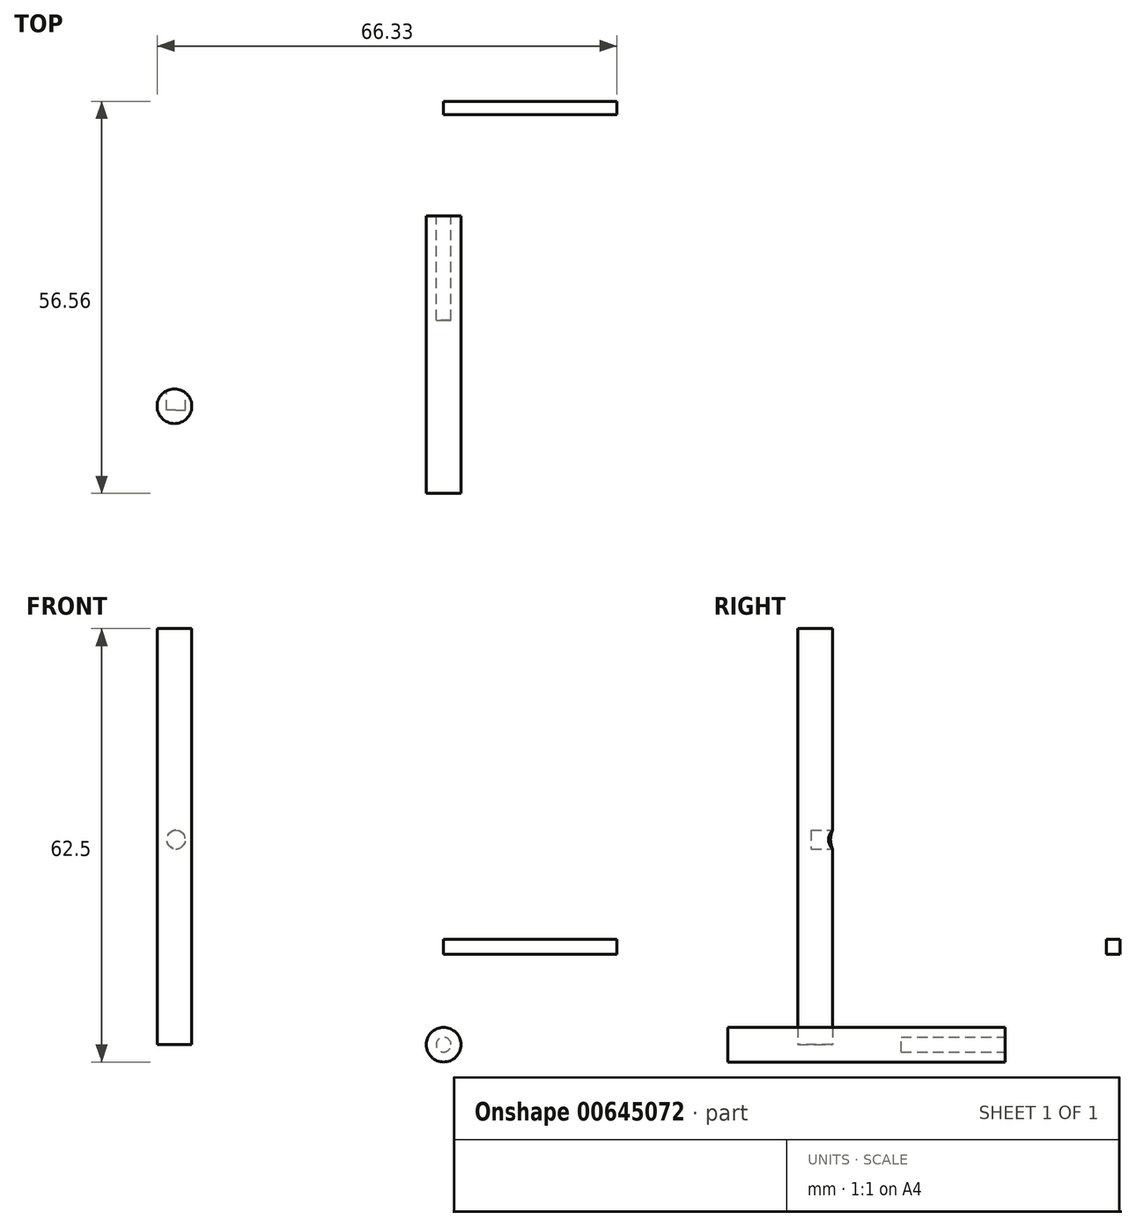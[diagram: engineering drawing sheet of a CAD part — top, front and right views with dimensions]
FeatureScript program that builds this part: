
annotation { "Feature Type Name" : "Feature", "Feature Type Description" : "" }
export const myFeature = defineFeature(function(context is Context, id is Id, definition is map)
    precondition{}
    {
        {
            var Q0;
            Q0=qCreatedBy(makeId("Front.planeOp"),FACE);
            var sketch = newSketch(context, id + "F0", { "sketchPlane" : qUnion([Q0])});
            skCircle(sketch, "E0", {"center": v(0, 0) * mm, "radius": 2.5 * mm});
            skSolve(sketch);
        }
        {
            var Q0;
            Q0=makeQuery(id+"F0.imprint","IMPRINT",FACE,{"disambiguationData":[TD([[makeQuery(id+"F0.imprint","IMPRINT",EDGE,{"derivedFrom":sQuery(id+"F0.wireOp",EDGE,"E0")}),1.0]])]});
            extrude(context, id + "F1", {"entities" : qUnion([Q0]), "depth" : 40 * mm, "offsetDistance" : 25 * mm});
        }
        {
            var Q0;
            Q0=qCreatedBy(makeId("Top.planeOp"),FACE);
            var sketch = newSketch(context, id + "F2", { "sketchPlane" : qUnion([Q0])});
            skCircle(sketch, "E1", {"center": v(-38.83, -27.42) * mm, "radius": 2.5 * mm});
            skSolve(sketch);
        }
        {
            var Q0;
            Q0=makeQuery(id+"F2.imprint","IMPRINT",FACE,{"disambiguationData":[TD([[makeQuery(id+"F2.imprint","IMPRINT",EDGE,{"derivedFrom":sQuery(id+"F2.wireOp",EDGE,"E1")}),1.0]])]});
            extrude(context, id + "F3", {"entities" : qUnion([Q0]), "depth" : 60 * mm, "offsetDistance" : 25 * mm});
        }
        {
            var Q0;
            Q0=qCreatedBy(makeId("Front.planeOp"),FACE);
            var sketch = newSketch(context, id + "F4", { "sketchPlane" : qUnion([Q0])});
            skCircle(sketch, "E2", {"center": v(0, 0) * mm, "radius": 1.07 * mm});
            skSolve(sketch);
        }
        {
            var Q0;
            Q0=makeQuery(id+"F4.imprint","IMPRINT",FACE,{"disambiguationData":[TD([[makeQuery(id+"F4.imprint","IMPRINT",EDGE,{"derivedFrom":sQuery(id+"F4.wireOp",EDGE,"E2")}),1.0]])]});
            extrude(context, id + "F5", {"entities" : qUnion([Q0]), "operationType" : NewBodyOperationType.REMOVE, "depth" : 15 * mm, "offsetDistance" : 25 * mm});
        }
        {
            var Q0;
            Q0=qCreatedBy(makeId("Front.planeOp"),FACE);
            var sketch = newSketch(context, id + "F6", { "sketchPlane" : qUnion([Q0])});
            skCircle(sketch, "E3", {"center": v(-38.6, 29.57) * mm, "radius": 1.34 * mm});
            skSolve(sketch);
        }
        {
            var Q0;
            Q0=makeQuery(id+"F6.imprint","IMPRINT",FACE,{"disambiguationData":[TD([[makeQuery(id+"F6.imprint","IMPRINT",EDGE,{"derivedFrom":sQuery(id+"F6.wireOp",EDGE,"E3")}),1.0]])]});
            extrude(context, id + "F7", {"entities" : qUnion([Q0]), "operationType" : NewBodyOperationType.REMOVE, "depth" : 28 * mm, "offsetDistance" : 25 * mm});
        }
        {
            var Q0;
            Q0=qCreatedBy(makeId("Right.planeOp"),FACE);
            var sketch = newSketch(context, id + "F8", { "sketchPlane" : qUnion([Q0])});
            skLineSegment(sketch, "E4.bottom", {"start": v(14.62, 15.22) * mm, "end": v(16.56, 15.22) * mm});
            skLineSegment(sketch, "E4.top", {"start": v(14.62, 13.06) * mm, "end": v(16.56, 13.06) * mm});
            skLineSegment(sketch, "E4.left", {"start": v(14.62, 15.22) * mm, "end": v(14.62, 13.06) * mm});
            skLineSegment(sketch, "E4.right", {"start": v(16.56, 15.22) * mm, "end": v(16.56, 13.06) * mm});
            skSolve(sketch);
        }
        {
            var Q0;
            Q0=makeQuery(id+"F8.imprint","IMPRINT",FACE,{"disambiguationData":[TD([[makeQuery(id+"F8.imprint","IMPRINT",EDGE,{"derivedFrom":sQuery(id+"F8.wireOp",EDGE,"E4.bottom")}),-1.0]])]});
            extrude(context, id + "F9", {"entities" : qUnion([Q0]), "depth" : 25 * mm, "offsetDistance" : 25 * mm});
        }
    });
